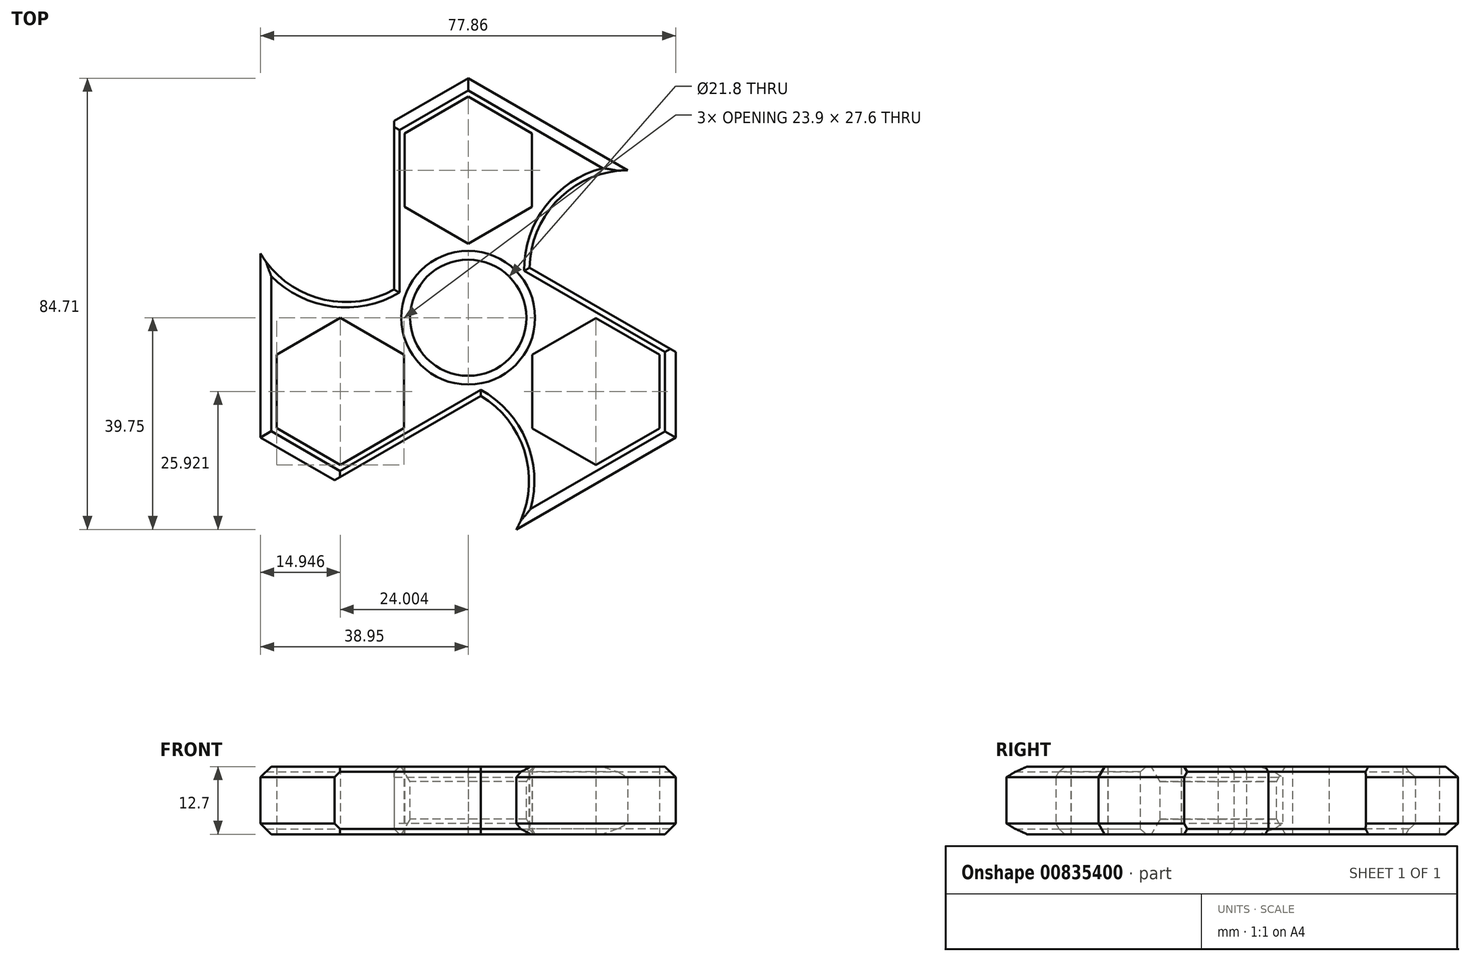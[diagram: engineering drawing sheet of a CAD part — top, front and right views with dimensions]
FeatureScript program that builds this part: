
annotation { "Feature Type Name" : "Feature", "Feature Type Description" : "" }
export const myFeature = defineFeature(function(context is Context, id is Id, definition is map)
    precondition{}
    {
        {
            var Q0;
            Q0=qCreatedBy(makeId("Top.planeOp"),FACE);
            var sketch = newSketch(context, id + "F0", { "sketchPlane" : qUnion([Q0])});
            skCircle(sketch, "E0", {"center": v(0, 0) * mm, "radius": 10.9 * mm});
            skSolve(sketch);
        }
        {
            var Q0;
            Q0=qCreatedBy(makeId("Top.planeOp"),FACE);
            var sketch = newSketch(context, id + "F1", { "sketchPlane" : qUnion([Q0])});
            skCircle(sketch, "E1.0", {"center": v(0, 0) * mm, "radius": 13.9 * mm});
            skCircle(sketch, "E2.cCircle", {"center": v(0, 27.7) * mm, "radius": 13.8 * mm, "construction": true});
            skLineSegment(sketch, "E2.0", {"start": v(11.95, 20.8) * mm, "end": v(0, 13.9) * mm});
            skLineSegment(sketch, "E2.1", {"start": v(0, 13.9) * mm, "end": v(-11.95, 20.8) * mm});
            skLineSegment(sketch, "E2.2", {"start": v(-11.95, 20.8) * mm, "end": v(-11.95, 34.6) * mm});
            skLineSegment(sketch, "E2.3", {"start": v(-11.95, 34.6) * mm, "end": v(0, 41.5) * mm});
            skLineSegment(sketch, "E2.4", {"start": v(0, 41.5) * mm, "end": v(11.95, 34.6) * mm});
            skLineSegment(sketch, "E2.5", {"start": v(11.95, 34.6) * mm, "end": v(11.95, 20.8) * mm});
            skLineSegment(sketch, "E3", {"start": v(-13.9, 5.3) * mm, "end": v(-13.9, 36.94) * mm});
            skLineSegment(sketch, "E4", {"start": v(-13.9, 36.94) * mm, "end": v(0, 44.96) * mm});
            skLineSegment(sketch, "E5", {"start": v(0, 44.96) * mm, "end": v(29.9, 27.7) * mm});
            skLineSegment(sketch, "E6", {"start": v(0, 27.7) * mm, "end": v(29.9, 27.7) * mm, "construction": true});
            skCircle(sketch, "E7", {"center": v(13.9, 0) * mm, "radius": 27.8 * mm, "construction": true});
            skArc(sketch, "E8.trimOffspring", {"start": v(29.9, 27.7) * mm, "mid": v(16.98, 22.28) * mm, "end": v(11.51, 9.38) * mm});
            skPoint(sketch, "E9.center.orphan", {"position": v(41.7, 0) * mm});
            skPoint(sketch, "E10.orphan", {"position": v(11.57, 7.7) * mm});
            skArc(sketch, "E11.1.0", {"start": v(-38.95, 12.06) * mm, "mid": v(-27.8, 3.59) * mm, "end": v(-13.9, 5.3) * mm});
            skLineSegment(sketch, "E11.1.1", {"start": v(-38.95, -22.46) * mm, "end": v(-38.95, 12.06) * mm});
            skLineSegment(sketch, "E11.1.2", {"start": v(-25.05, -30.49) * mm, "end": v(-38.95, -22.46) * mm});
            skLineSegment(sketch, "E11.1.3", {"start": v(2.34, -14.67) * mm, "end": v(-25.05, -30.49) * mm});
            skLineSegment(sketch, "E11.1.4", {"start": v(-35.95, -20.73) * mm, "end": v(-35.95, -6.93) * mm});
            skLineSegment(sketch, "E11.1.5", {"start": v(-24, -27.63) * mm, "end": v(-35.95, -20.73) * mm});
            skLineSegment(sketch, "E11.1.6", {"start": v(-12.05, -20.73) * mm, "end": v(-24, -27.63) * mm});
            skLineSegment(sketch, "E11.1.7", {"start": v(-12.05, -6.93) * mm, "end": v(-12.05, -20.73) * mm});
            skLineSegment(sketch, "E11.1.8", {"start": v(-24, -0.03) * mm, "end": v(-12.05, -6.93) * mm});
            skLineSegment(sketch, "E11.1.9", {"start": v(-35.95, -6.93) * mm, "end": v(-24, -0.03) * mm});
            skArc(sketch, "E11.2.0", {"start": v(9.01, -39.75) * mm, "mid": v(10.78, -25.85) * mm, "end": v(2.34, -14.67) * mm});
            skLineSegment(sketch, "E11.2.1", {"start": v(38.91, -22.48) * mm, "end": v(9.01, -39.75) * mm});
            skLineSegment(sketch, "E11.2.2", {"start": v(38.91, -6.43) * mm, "end": v(38.91, -22.48) * mm});
            skLineSegment(sketch, "E11.2.3", {"start": v(11.51, 9.38) * mm, "end": v(38.91, -6.43) * mm});
            skLineSegment(sketch, "E11.2.4", {"start": v(35.91, -20.75) * mm, "end": v(23.96, -27.65) * mm});
            skLineSegment(sketch, "E11.2.5", {"start": v(35.91, -6.95) * mm, "end": v(35.91, -20.75) * mm});
            skLineSegment(sketch, "E11.2.6", {"start": v(23.96, -0.05) * mm, "end": v(35.91, -6.95) * mm});
            skLineSegment(sketch, "E11.2.7", {"start": v(12.01, -6.95) * mm, "end": v(23.96, -0.05) * mm});
            skLineSegment(sketch, "E11.2.8", {"start": v(12.01, -20.75) * mm, "end": v(12.01, -6.95) * mm});
            skLineSegment(sketch, "E11.2.9", {"start": v(23.96, -27.65) * mm, "end": v(12.01, -20.75) * mm});
            skPoint(sketch, "E11.center", {"position": v(-0.01, 0) * mm});
            skPoint(sketch, "E12", {"position": v(11.51, 9.38) * mm});
            skPoint(sketch, "E13", {"position": v(2.34, -14.67) * mm});
            skPoint(sketch, "E14.orphan", {"position": v(-12.48, 6.18) * mm});
            skPoint(sketch, "E15.orphan", {"position": v(-13.9, 0) * mm});
            skPoint(sketch, "E16.orphan", {"position": v(0.87, -13.88) * mm});
            skPoint(sketch, "E17.orphan", {"position": v(6.93, -12.02) * mm});
            skPoint(sketch, "E18.orphan", {"position": v(6.92, 12.03) * mm});
            skSolve(sketch);
        }
        {
            var Q0;
            {var subQ2=sQuery(id+"F1.wireOp",EDGE,"E2.0");Q0=makeQuery(id+"F1.imprint","IMPRINT",FACE,{"disambiguationData":[TD([[makeQuery(id+"F1.imprint","IMPRINT",EDGE,{"derivedFrom":subQ2}),1.0]])]});}
            var Q1;
            {var subQ0=sQuery(id+"F1.wireOp",EDGE,"E1.0");var subQ1=makeQuery(id+"F1.imprint","INTERSECT",VERTEX,{"derivedFrom":[subQ0,sQuery(id+"F1.wireOp",EDGE,"E2.0"),sQuery(id+"F1.wireOp",EDGE,"E2.1")]});Q1=makeQuery(id+"F1.imprint","IMPRINT",FACE,{"disambiguationData":[TD([[makeQuery(id+"F1.imprint","IMPRINT",EDGE,{"disambiguationData":[TD([[subQ1,-1.0]])],"derivedFrom":subQ0}),1.0]])]});}
            extrude(context, id + "F2", {"entities" : qUnion([Q0, Q1]), "endBound" : BoundingType.SYMMETRIC, "depth" : 12.7 * mm, "offsetDistance" : 25 * mm});
        }
        {
            var Q0;
            Q0=makeQuery(id+"F0.imprint","IMPRINT",FACE,{"disambiguationData":[TD([[makeQuery(id+"F0.imprint","IMPRINT",EDGE,{"derivedFrom":sQuery(id+"F0.wireOp",EDGE,"E0")}),1.0]])]});
            extrude(context, id + "F3", {"entities" : qUnion([Q0]), "operationType" : NewBodyOperationType.REMOVE, "endBound" : BoundingType.SYMMETRIC, "oppositeDirection" : true, "depth" : 25 * mm, "offsetDistance" : 25 * mm});
        }
        {
            var Q0;
            Q0=makeQuery(id+"F2.opExtrude","CAP_EDGE",EDGE,{"disambiguationData":[OSD([sQuery(id+"F1.wireOp",EDGE,"E5")])],"isStart":true});
            var Q1;
            Q1=makeQuery(id+"F2.opExtrude","CAP_EDGE",EDGE,{"disambiguationData":[OSD([sQuery(id+"F1.wireOp",EDGE,"E5")])],"isStart":false});
            var Q2;
            Q2=makeQuery(id+"F2.opExtrude","CAP_EDGE",EDGE,{"disambiguationData":[OSD([sQuery(id+"F1.wireOp",EDGE,"E11.1.1")])],"isStart":false});
            var Q3;
            Q3=makeQuery(id+"F2.opExtrude","CAP_EDGE",EDGE,{"disambiguationData":[OSD([sQuery(id+"F1.wireOp",EDGE,"E11.1.1")])],"isStart":true});
            var Q4;
            Q4=makeQuery(id+"F2.opExtrude","CAP_EDGE",EDGE,{"disambiguationData":[OSD([sQuery(id+"F1.wireOp",EDGE,"E11.1.2")])],"isStart":true});
            var Q5;
            Q5=makeQuery(id+"F2.opExtrude","CAP_EDGE",EDGE,{"disambiguationData":[OSD([sQuery(id+"F1.wireOp",EDGE,"E11.1.2")])],"isStart":false});
            var Q6;
            Q6=makeQuery(id+"F2.opExtrude","CAP_EDGE",EDGE,{"disambiguationData":[OSD([sQuery(id+"F1.wireOp",EDGE,"E11.2.1")])],"isStart":true});
            var Q7;
            Q7=makeQuery(id+"F2.opExtrude","CAP_EDGE",EDGE,{"disambiguationData":[OSD([sQuery(id+"F1.wireOp",EDGE,"E11.2.1")])],"isStart":false});
            var Q8;
            Q8=makeQuery(id+"F2.opExtrude","CAP_EDGE",EDGE,{"disambiguationData":[OSD([sQuery(id+"F1.wireOp",EDGE,"E11.2.2")])],"isStart":false});
            var Q9;
            Q9=makeQuery(id+"F2.opExtrude","CAP_EDGE",EDGE,{"disambiguationData":[OSD([sQuery(id+"F1.wireOp",EDGE,"E11.2.2")])],"isStart":true});
            var Q10;
            Q10=makeQuery(id+"F2.opExtrude","CAP_EDGE",EDGE,{"disambiguationData":[OSD([sQuery(id+"F1.wireOp",EDGE,"E4")])],"isStart":true});
            var Q11;
            Q11=makeQuery(id+"F2.opExtrude","CAP_EDGE",EDGE,{"disambiguationData":[OSD([sQuery(id+"F1.wireOp",EDGE,"E4")])],"isStart":false});
            chamfer(context, id + "F4", {"entities" : qUnion([Q0, Q1, Q2, Q3, Q4, Q5, Q6, Q7, Q8, Q9, Q10, Q11]), "width" : 2 * mm, "tangentPropagation" : true});
        }
        {
            var Q0;
            Q0=makeQuery(id+"F2.opExtrude","CAP_EDGE",EDGE,{"disambiguationData":[OSD([sQuery(id+"F1.wireOp",EDGE,"E11.1.3")])],"isStart":false});
            var Q1;
            Q1=makeQuery(id+"F2.opExtrude","CAP_EDGE",EDGE,{"disambiguationData":[OSD([sQuery(id+"F1.wireOp",EDGE,"E11.1.3")])],"isStart":true});
            var Q2;
            Q2=makeQuery(id+"F2.opExtrude","CAP_EDGE",EDGE,{"disambiguationData":[OSD([sQuery(id+"F1.wireOp",EDGE,"E3")])],"isStart":true});
            var Q3;
            Q3=makeQuery(id+"F2.opExtrude","CAP_EDGE",EDGE,{"disambiguationData":[OSD([sQuery(id+"F1.wireOp",EDGE,"E3")])],"isStart":false});
            var Q4;
            Q4=makeQuery(id+"F2.opExtrude","CAP_EDGE",EDGE,{"disambiguationData":[OSD([sQuery(id+"F1.wireOp",EDGE,"E11.2.3")])],"isStart":false});
            var Q5;
            Q5=makeQuery(id+"F2.opExtrude","CAP_EDGE",EDGE,{"disambiguationData":[OSD([sQuery(id+"F1.wireOp",EDGE,"E11.2.3")])],"isStart":true});
            var Q6;
            Q6=makeQuery(id+"F2.opExtrude","CAP_EDGE",EDGE,{"disambiguationData":[OSD([sQuery(id+"F1.wireOp",EDGE,"E8.trimOffspring")])],"isStart":false});
            var Q7;
            Q7=makeQuery(id+"F2.opExtrude","CAP_EDGE",EDGE,{"disambiguationData":[OSD([sQuery(id+"F1.wireOp",EDGE,"E8.trimOffspring")])],"isStart":true});
            var Q8;
            Q8=makeQuery(id+"F2.opExtrude","CAP_EDGE",EDGE,{"disambiguationData":[OSD([sQuery(id+"F1.wireOp",EDGE,"E11.1.0")])],"isStart":false});
            var Q9;
            Q9=makeQuery(id+"F2.opExtrude","CAP_EDGE",EDGE,{"disambiguationData":[OSD([sQuery(id+"F1.wireOp",EDGE,"E11.1.0")])],"isStart":true});
            var Q10;
            Q10=makeQuery(id+"F2.opExtrude","CAP_EDGE",EDGE,{"disambiguationData":[OSD([sQuery(id+"F1.wireOp",EDGE,"E11.2.0")])],"isStart":true});
            var Q11;
            Q11=makeQuery(id+"F2.opExtrude","CAP_EDGE",EDGE,{"disambiguationData":[OSD([sQuery(id+"F1.wireOp",EDGE,"E11.2.0")])],"isStart":false});
            chamfer(context, id + "F5", {"entities" : qUnion([Q0, Q1, Q2, Q3, Q4, Q5, Q6, Q7, Q8, Q9, Q10, Q11]), "width" : 1 * mm, "tangentPropagation" : true});
        }
        {
            var Q0;
            Q0=makeQuery(id+"F3.boolean.opBoolean","INTERSECT",EDGE,{"derivedFrom":[makeQuery(id+"F2.opExtrude","CAP_FACE",FACE,{"disambiguationData":[OSD([sQuery(id+"F1.wireOp",EDGE,"E2.0"),sQuery(id+"F1.wireOp",EDGE,"E2.1"),sQuery(id+"F1.wireOp",EDGE,"E2.2"),sQuery(id+"F1.wireOp",EDGE,"E2.3"),sQuery(id+"F1.wireOp",EDGE,"E2.4"),sQuery(id+"F1.wireOp",EDGE,"E2.5"),sQuery(id+"F1.wireOp",EDGE,"E3"),sQuery(id+"F1.wireOp",EDGE,"E4"),sQuery(id+"F1.wireOp",EDGE,"E5"),sQuery(id+"F1.wireOp",EDGE,"E8.trimOffspring"),sQuery(id+"F1.wireOp",EDGE,"E11.1.0"),sQuery(id+"F1.wireOp",EDGE,"E11.1.1"),sQuery(id+"F1.wireOp",EDGE,"E11.1.2"),sQuery(id+"F1.wireOp",EDGE,"E11.1.3"),sQuery(id+"F1.wireOp",EDGE,"E11.1.4"),sQuery(id+"F1.wireOp",EDGE,"E11.1.5"),sQuery(id+"F1.wireOp",EDGE,"E11.1.6"),sQuery(id+"F1.wireOp",EDGE,"E11.1.7"),sQuery(id+"F1.wireOp",EDGE,"E11.1.8"),sQuery(id+"F1.wireOp",EDGE,"E11.1.9"),sQuery(id+"F1.wireOp",EDGE,"E11.2.0"),sQuery(id+"F1.wireOp",EDGE,"E11.2.1"),sQuery(id+"F1.wireOp",EDGE,"E11.2.2"),sQuery(id+"F1.wireOp",EDGE,"E11.2.3"),sQuery(id+"F1.wireOp",EDGE,"E11.2.4"),sQuery(id+"F1.wireOp",EDGE,"E11.2.5"),sQuery(id+"F1.wireOp",EDGE,"E11.2.6"),sQuery(id+"F1.wireOp",EDGE,"E11.2.7"),sQuery(id+"F1.wireOp",EDGE,"E11.2.8"),sQuery(id+"F1.wireOp",EDGE,"E11.2.9")])],"isStart":false}),makeQuery(id+"F3.opExtrude","SWEPT_FACE",FACE,{"disambiguationData":[OSD([sQuery(id+"F0.wireOp",EDGE,"E0")])]})]});
            var Q1;
            Q1=makeQuery(id+"F3.boolean.opBoolean","INTERSECT",EDGE,{"derivedFrom":[makeQuery(id+"F2.opExtrude","CAP_FACE",FACE,{"disambiguationData":[OSD([sQuery(id+"F1.wireOp",EDGE,"E2.0"),sQuery(id+"F1.wireOp",EDGE,"E2.1"),sQuery(id+"F1.wireOp",EDGE,"E2.2"),sQuery(id+"F1.wireOp",EDGE,"E2.3"),sQuery(id+"F1.wireOp",EDGE,"E2.4"),sQuery(id+"F1.wireOp",EDGE,"E2.5"),sQuery(id+"F1.wireOp",EDGE,"E3"),sQuery(id+"F1.wireOp",EDGE,"E4"),sQuery(id+"F1.wireOp",EDGE,"E5"),sQuery(id+"F1.wireOp",EDGE,"E8.trimOffspring"),sQuery(id+"F1.wireOp",EDGE,"E11.1.0"),sQuery(id+"F1.wireOp",EDGE,"E11.1.1"),sQuery(id+"F1.wireOp",EDGE,"E11.1.2"),sQuery(id+"F1.wireOp",EDGE,"E11.1.3"),sQuery(id+"F1.wireOp",EDGE,"E11.1.4"),sQuery(id+"F1.wireOp",EDGE,"E11.1.5"),sQuery(id+"F1.wireOp",EDGE,"E11.1.6"),sQuery(id+"F1.wireOp",EDGE,"E11.1.7"),sQuery(id+"F1.wireOp",EDGE,"E11.1.8"),sQuery(id+"F1.wireOp",EDGE,"E11.1.9"),sQuery(id+"F1.wireOp",EDGE,"E11.2.0"),sQuery(id+"F1.wireOp",EDGE,"E11.2.1"),sQuery(id+"F1.wireOp",EDGE,"E11.2.2"),sQuery(id+"F1.wireOp",EDGE,"E11.2.3"),sQuery(id+"F1.wireOp",EDGE,"E11.2.4"),sQuery(id+"F1.wireOp",EDGE,"E11.2.5"),sQuery(id+"F1.wireOp",EDGE,"E11.2.6"),sQuery(id+"F1.wireOp",EDGE,"E11.2.7"),sQuery(id+"F1.wireOp",EDGE,"E11.2.8"),sQuery(id+"F1.wireOp",EDGE,"E11.2.9")])],"isStart":true}),makeQuery(id+"F3.opExtrude","SWEPT_FACE",FACE,{"disambiguationData":[OSD([sQuery(id+"F0.wireOp",EDGE,"E0")])]})]});
            chamfer(context, id + "F6", {"entities" : qUnion([Q0, Q1]), "chamferType" : ChamferType.OFFSET_ANGLE, "width" : 2.85 * mm, "oppositeDirection" : false, "angle" : 30 * degree, "tangentPropagation" : true});
        }
    });
